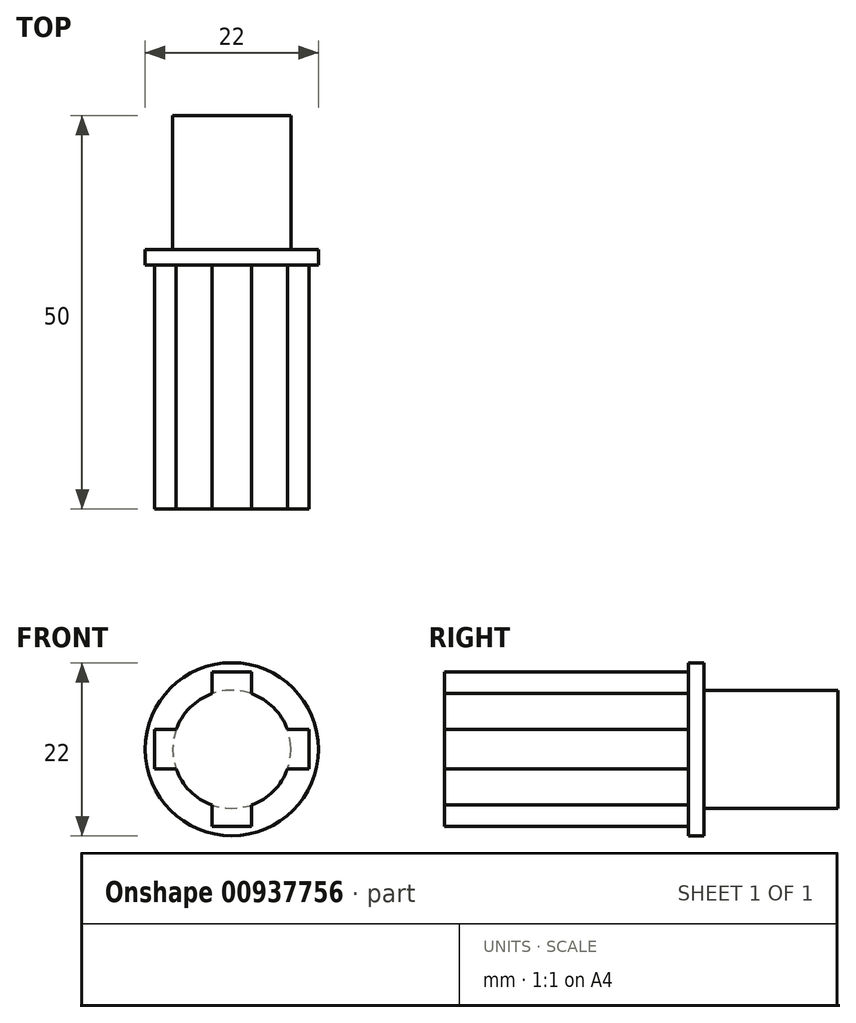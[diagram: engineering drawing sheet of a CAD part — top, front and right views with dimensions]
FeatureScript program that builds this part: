
annotation { "Feature Type Name" : "Feature", "Feature Type Description" : "" }
export const myFeature = defineFeature(function(context is Context, id is Id, definition is map)
    precondition{}
    {
        {
            var Q0;
            Q0=qCreatedBy(makeId("Front.planeOp"),FACE);
            var sketch = newSketch(context, id + "F0", { "sketchPlane" : qUnion([Q0])});
            skCircle(sketch, "E0", {"center": v(0, 0) * mm, "radius": 7.5 * mm});
            skSolve(sketch);
        }
        {
            var Q0;
            Q0=qSketchRegion(id+"F0",true);
            extrude(context, id + "F1", {"entities" : qUnion([Q0]), "depth" : 17 * mm, "offsetDistance" : 25 * mm});
        }
        {
            var Q0;
            Q0=makeQuery(id+"F1.opExtrude","CAP_FACE",FACE,{"disambiguationData":[OSD([sQuery(id+"F0.wireOp",EDGE,"E0")])],"isStart":false});
            var sketch = newSketch(context, id + "F2", { "sketchPlane" : qUnion([Q0])});
            skCircle(sketch, "E1", {"center": v(0, 0) * mm, "radius": 11 * mm});
            skSolve(sketch);
        }
        {
            var Q0;
            Q0=qSketchRegion(id+"F2",true);
            extrude(context, id + "F3", {"entities" : qUnion([Q0]), "operationType" : NewBodyOperationType.ADD, "depth" : 2 * mm, "offsetDistance" : 25 * mm});
        }
        {
            var Q0;
            Q0=makeQuery(id+"F3.opExtrude","CAP_FACE",FACE,{"disambiguationData":[OSD([sQuery(id+"F2.wireOp",EDGE,"E1")])],"isStart":false});
            var sketch = newSketch(context, id + "F4", { "sketchPlane" : qUnion([Q0])});
            skCircle(sketch, "E2", {"center": v(0, 0) * mm, "radius": 11 * mm});
            skCircle(sketch, "E3", {"center": v(0, 0) * mm, "radius": 7.5 * mm});
            skLineSegment(sketch, "E4", {"start": v(0, 9.8) * mm, "end": v(-2.5, 9.8) * mm});
            skLineSegment(sketch, "E5", {"start": v(0, 9.8) * mm, "end": v(2.5, 9.8) * mm});
            skLineSegment(sketch, "E6", {"start": v(2.5, 9.8) * mm, "end": v(2.5, 7.07) * mm});
            skLineSegment(sketch, "E7", {"start": v(-2.5, 9.8) * mm, "end": v(-2.5, 7.07) * mm});
            skLineSegment(sketch, "E8.1.0", {"start": v(-9.8, 0) * mm, "end": v(-9.8, 2.5) * mm});
            skLineSegment(sketch, "E8.1.1", {"start": v(-9.8, 2.5) * mm, "end": v(-7.07, 2.5) * mm});
            skLineSegment(sketch, "E8.1.2", {"start": v(-9.8, 0) * mm, "end": v(-9.8, -2.5) * mm});
            skLineSegment(sketch, "E8.1.3", {"start": v(-9.8, -2.5) * mm, "end": v(-7.07, -2.5) * mm});
            skLineSegment(sketch, "E8.2.0", {"start": v(0, -9.8) * mm, "end": v(-2.5, -9.8) * mm});
            skLineSegment(sketch, "E8.2.1", {"start": v(-2.5, -9.8) * mm, "end": v(-2.5, -7.07) * mm});
            skLineSegment(sketch, "E8.2.2", {"start": v(0, -9.8) * mm, "end": v(2.5, -9.8) * mm});
            skLineSegment(sketch, "E8.2.3", {"start": v(2.5, -9.8) * mm, "end": v(2.5, -7.07) * mm});
            skLineSegment(sketch, "E8.3.0", {"start": v(9.8, 0) * mm, "end": v(9.8, -2.5) * mm});
            skLineSegment(sketch, "E8.3.1", {"start": v(9.8, -2.5) * mm, "end": v(7.07, -2.5) * mm});
            skLineSegment(sketch, "E8.3.2", {"start": v(9.8, 0) * mm, "end": v(9.8, 2.5) * mm});
            skLineSegment(sketch, "E8.3.3", {"start": v(9.8, 2.5) * mm, "end": v(7.07, 2.5) * mm});
            skSolve(sketch);
        }
        {
            var Q0;
            {var subQ0=sQuery(id+"F4.wireOp",EDGE,"E3");var subQ4=makeQuery(id+"F4.imprint","INTERSECT",VERTEX,{"derivedFrom":[subQ0,sQuery(id+"F4.wireOp",EDGE,"E6")]});Q0=makeQuery(id+"F4.imprint","IMPRINT",FACE,{"disambiguationData":[TD([[makeQuery(id+"F4.imprint","IMPRINT",EDGE,{"disambiguationData":[TD([[subQ4,1.0]])],"derivedFrom":subQ0}),1.0]])]});}
            var Q1;
            Q1=makeQuery(id+"F4.imprint","IMPRINT",FACE,{"disambiguationData":[TD([[makeQuery(id+"F4.imprint","IMPRINT",EDGE,{"derivedFrom":sQuery(id+"F4.wireOp",EDGE,"E8.3.0")}),-1.0]])]});
            var Q2;
            Q2=makeQuery(id+"F4.imprint","IMPRINT",FACE,{"disambiguationData":[TD([[makeQuery(id+"F4.imprint","IMPRINT",EDGE,{"derivedFrom":sQuery(id+"F4.wireOp",EDGE,"E4")}),1.0]])]});
            var Q3;
            Q3=makeQuery(id+"F4.imprint","IMPRINT",FACE,{"disambiguationData":[TD([[makeQuery(id+"F4.imprint","IMPRINT",EDGE,{"derivedFrom":sQuery(id+"F4.wireOp",EDGE,"E8.1.0")}),-1.0]])]});
            var Q4;
            Q4=makeQuery(id+"F4.imprint","IMPRINT",FACE,{"disambiguationData":[TD([[makeQuery(id+"F4.imprint","IMPRINT",EDGE,{"derivedFrom":sQuery(id+"F4.wireOp",EDGE,"E8.2.0")}),-1.0]])]});
            extrude(context, id + "F5", {"entities" : qUnion([Q0, Q1, Q2, Q3, Q4]), "depth" : 31 * mm, "offsetDistance" : 25 * mm});
        }
    });
